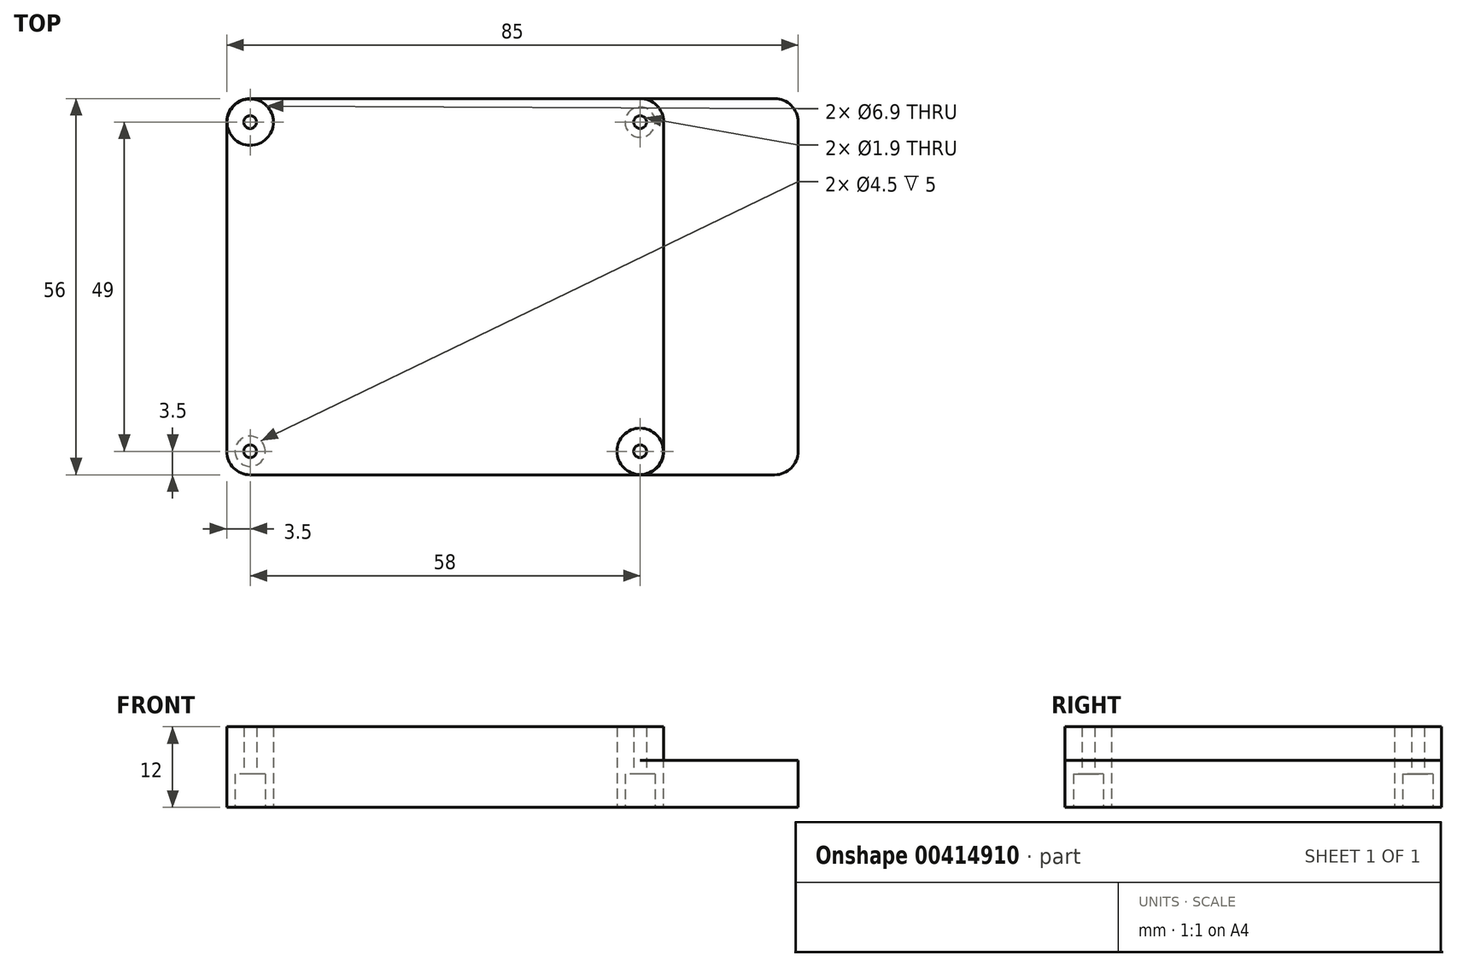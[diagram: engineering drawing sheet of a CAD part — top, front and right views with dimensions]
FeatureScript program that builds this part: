
annotation { "Feature Type Name" : "Feature", "Feature Type Description" : "" }
export const myFeature = defineFeature(function(context is Context, id is Id, definition is map)
    precondition{}
    {
        {
            var Q0;
            Q0=qCreatedBy(makeId("Top.planeOp"),FACE);
            var sketch = newSketch(context, id + "F0", { "sketchPlane" : qUnion([Q0])});
            skLineSegment(sketch, "E0.bottom", {"start": v(3.5, 0) * mm, "end": v(81.5, 0) * mm});
            skLineSegment(sketch, "E0.top", {"start": v(3.5, 56) * mm, "end": v(81.5, 56) * mm});
            skLineSegment(sketch, "E0.left", {"start": v(0, 3.5) * mm, "end": v(0, 52.5) * mm});
            skLineSegment(sketch, "E0.right", {"start": v(85, 3.5) * mm, "end": v(85, 52.5) * mm});
            skPoint(sketch, "E1.visualSharp", {"position": v(0, 56) * mm});
            skArc(sketch, "E1.filletArc", {"start": v(3.5, 56) * mm, "mid": v(1.03, 54.97) * mm, "end": v(0, 52.5) * mm});
            skPoint(sketch, "E2.visualSharp", {"position": v(85, 56) * mm});
            skArc(sketch, "E2.filletArc", {"start": v(85, 52.5) * mm, "mid": v(83.97, 54.97) * mm, "end": v(81.5, 56) * mm});
            skPoint(sketch, "E3.visualSharp", {"position": v(85, 0) * mm});
            skArc(sketch, "E3.filletArc", {"start": v(81.5, 0) * mm, "mid": v(83.97, 1.03) * mm, "end": v(85, 3.5) * mm});
            skPoint(sketch, "E4.visualSharp", {"position": v(0, 0) * mm});
            skArc(sketch, "E4.filletArc", {"start": v(0, 3.5) * mm, "mid": v(1.03, 1.03) * mm, "end": v(3.5, 0) * mm});
            skLineSegment(sketch, "E5", {"start": v(0, 28) * mm, "end": v(85, 28) * mm, "construction": true});
            skLineSegment(sketch, "E6", {"start": v(3.5, 56) * mm, "end": v(3.5, 0) * mm, "construction": true});
            skLineSegment(sketch, "E7", {"start": v(61.5, 56) * mm, "end": v(61.5, 0) * mm, "construction": true});
            skLineSegment(sketch, "E8", {"start": v(-3.04, 52.5) * mm, "end": v(0, 52.5) * mm, "construction": true});
            skLineSegment(sketch, "E9", {"start": v(-4.07, 3.5) * mm, "end": v(0, 3.5) * mm, "construction": true});
            skCircle(sketch, "E10", {"center": v(3.5, 3.5) * mm, "radius": 0.95 * mm});
            skCircle(sketch, "E11", {"center": v(3.5, 3.5) * mm, "radius": 3.45 * mm});
            skCircle(sketch, "E12.MirrorC", {"center": v(3.5, 52.5) * mm, "radius": 3.45 * mm});
            skCircle(sketch, "E13.MirrorC", {"center": v(3.5, 52.5) * mm, "radius": 0.95 * mm});
            skLineSegment(sketch, "E14", {"start": v(32.5, 56) * mm, "end": v(32.5, 0) * mm, "construction": true});
            skCircle(sketch, "E15.MirrorC", {"center": v(61.5, 52.5) * mm, "radius": 3.45 * mm});
            skCircle(sketch, "E16.MirrorC", {"center": v(61.5, 52.5) * mm, "radius": 0.95 * mm});
            skCircle(sketch, "E17.MirrorC", {"center": v(61.5, 3.5) * mm, "radius": 0.95 * mm});
            skCircle(sketch, "E18.MirrorC", {"center": v(61.5, 3.5) * mm, "radius": 3.45 * mm});
            skCircle(sketch, "E19", {"center": v(3.5, 3.5) * mm, "radius": 2.25 * mm});
            skCircle(sketch, "E20.MirrorC", {"center": v(3.5, 52.5) * mm, "radius": 2.25 * mm});
            skCircle(sketch, "E21.MirrorC", {"center": v(61.5, 52.5) * mm, "radius": 2.25 * mm});
            skCircle(sketch, "E22.MirrorC", {"center": v(61.5, 3.5) * mm, "radius": 2.25 * mm});
            skSolve(sketch);
        }
        {
            var Q0;
            Q0=qCreatedBy(makeId("Top.planeOp"),FACE);
            var sketch = newSketch(context, id + "F1", { "sketchPlane" : qUnion([Q0])});
            skLineSegment(sketch, "E23.bottom", {"start": v(3.5, 0) * mm, "end": v(61.5, 0) * mm});
            skLineSegment(sketch, "E23.top", {"start": v(3.5, 56) * mm, "end": v(61.5, 56) * mm});
            skLineSegment(sketch, "E23.left", {"start": v(0, 3.5) * mm, "end": v(0, 52.5) * mm});
            skLineSegment(sketch, "E23.right", {"start": v(65, 3.5) * mm, "end": v(65, 52.5) * mm});
            skPoint(sketch, "E24.visualSharp", {"position": v(0, 56) * mm});
            skArc(sketch, "E24.filletArc", {"start": v(3.5, 56) * mm, "mid": v(1.03, 54.97) * mm, "end": v(0, 52.5) * mm});
            skPoint(sketch, "E25.visualSharp", {"position": v(65, 56) * mm});
            skArc(sketch, "E25.filletArc", {"start": v(65, 52.5) * mm, "mid": v(63.97, 54.97) * mm, "end": v(61.5, 56) * mm});
            skPoint(sketch, "E26.visualSharp", {"position": v(65, 0) * mm});
            skArc(sketch, "E26.filletArc", {"start": v(61.5, 0) * mm, "mid": v(63.97, 1.03) * mm, "end": v(65, 3.5) * mm});
            skPoint(sketch, "E27.visualSharp", {"position": v(0, 0) * mm});
            skArc(sketch, "E27.filletArc", {"start": v(0, 3.5) * mm, "mid": v(1.03, 1.03) * mm, "end": v(3.5, 0) * mm});
            skLineSegment(sketch, "E28", {"start": v(0, 28) * mm, "end": v(65, 28) * mm, "construction": true});
            skLineSegment(sketch, "E29", {"start": v(3.5, 56) * mm, "end": v(3.5, 0) * mm, "construction": true});
            skLineSegment(sketch, "E30", {"start": v(61.5, 56) * mm, "end": v(61.5, 0) * mm, "construction": true});
            skLineSegment(sketch, "E31", {"start": v(-37.6, 52.5) * mm, "end": v(0, 52.5) * mm, "construction": true});
            skLineSegment(sketch, "E32", {"start": v(-38.61, 3.5) * mm, "end": v(0, 3.5) * mm, "construction": true});
            skCircle(sketch, "E33", {"center": v(3.5, 3.5) * mm, "radius": 0.95 * mm});
            skCircle(sketch, "E34", {"center": v(3.5, 3.5) * mm, "radius": 3.45 * mm});
            skCircle(sketch, "E35.MirrorC", {"center": v(3.5, 52.5) * mm, "radius": 3.45 * mm});
            skCircle(sketch, "E36.MirrorC", {"center": v(3.5, 52.5) * mm, "radius": 0.95 * mm});
            skLineSegment(sketch, "E37", {"start": v(32.5, 56) * mm, "end": v(32.5, 0) * mm, "construction": true});
            skCircle(sketch, "E38.MirrorC", {"center": v(61.5, 52.5) * mm, "radius": 3.45 * mm});
            skCircle(sketch, "E39.MirrorC", {"center": v(61.5, 52.5) * mm, "radius": 0.95 * mm});
            skCircle(sketch, "E40.MirrorC", {"center": v(61.5, 3.5) * mm, "radius": 0.95 * mm});
            skCircle(sketch, "E41.MirrorC", {"center": v(61.5, 3.5) * mm, "radius": 3.45 * mm});
            skCircle(sketch, "E42", {"center": v(3.5, 3.5) * mm, "radius": 2.25 * mm});
            skCircle(sketch, "E43.MirrorC", {"center": v(3.5, 52.5) * mm, "radius": 2.25 * mm});
            skCircle(sketch, "E44.MirrorC", {"center": v(61.5, 52.5) * mm, "radius": 2.25 * mm});
            skCircle(sketch, "E45.MirrorC", {"center": v(61.5, 3.5) * mm, "radius": 2.25 * mm});
            skSolve(sketch);
        }
        {
            var Q0;
            Q0=makeQuery(id+"F0.imprint","IMPRINT",FACE,{"disambiguationData":[TD([[makeQuery(id+"F0.imprint","IMPRINT",EDGE,{"derivedFrom":sQuery(id+"F0.wireOp",EDGE,"E0.bottom")}),1.0]])]});
            var Q1;
            Q1=makeQuery(id+"F0.imprint","IMPRINT",FACE,{"disambiguationData":[TD([[makeQuery(id+"F0.imprint","IMPRINT",EDGE,{"derivedFrom":sQuery(id+"F0.wireOp",EDGE,"E12.MirrorC")}),-1.0]])]});
            var Q2;
            Q2 = qSketchRegion(id + "F0", true);
            var Q3;
            Q3=makeQuery(id+"F0.imprint","IMPRINT",FACE,{"disambiguationData":[TD([[makeQuery(id+"F0.imprint","IMPRINT",EDGE,{"derivedFrom":sQuery(id+"F0.wireOp",EDGE,"E15.MirrorC")}),1.0]])]});
            var Q4;
            Q4=makeQuery(id+"F0.imprint","IMPRINT",FACE,{"disambiguationData":[TD([[makeQuery(id+"F0.imprint","IMPRINT",EDGE,{"derivedFrom":sQuery(id+"F0.wireOp",EDGE,"E18.MirrorC")}),-1.0]])]});
            var Q5;
            Q5=makeQuery(id+"F0.imprint","IMPRINT",FACE,{"disambiguationData":[TD([[makeQuery(id+"F0.imprint","IMPRINT",EDGE,{"derivedFrom":sQuery(id+"F0.wireOp",EDGE,"E11")}),1.0]])]});
            extrude(context, id + "F2", {"entities" : qUnion([Q0, Q1, Q2, Q3, Q4, Q5]), "depth" : 2 * mm});
        }
        {
            var Q0;
            Q0=makeQuery(id+"F0.imprint","IMPRINT",FACE,{"disambiguationData":[TD([[makeQuery(id+"F0.imprint","IMPRINT",EDGE,{"derivedFrom":sQuery(id+"F0.wireOp",EDGE,"E11")}),1.0]])]});
            var Q1;
            Q1=makeQuery(id+"F0.imprint","IMPRINT",FACE,{"disambiguationData":[TD([[makeQuery(id+"F0.imprint","IMPRINT",EDGE,{"derivedFrom":sQuery(id+"F0.wireOp",EDGE,"E12.MirrorC")}),-1.0]])]});
            var Q2;
            Q2=makeQuery(id+"F0.imprint","IMPRINT",FACE,{"disambiguationData":[TD([[makeQuery(id+"F0.imprint","IMPRINT",EDGE,{"derivedFrom":sQuery(id+"F0.wireOp",EDGE,"E18.MirrorC")}),-1.0]])]});
            var Q3;
            Q3=makeQuery(id+"F0.imprint","IMPRINT",FACE,{"disambiguationData":[TD([[makeQuery(id+"F0.imprint","IMPRINT",EDGE,{"derivedFrom":sQuery(id+"F0.wireOp",EDGE,"E15.MirrorC")}),1.0]])]});
            var Q4;
            Q4=makeQuery(id+"F0.imprint","IMPRINT",FACE,{"disambiguationData":[TD([[makeQuery(id+"F0.imprint","IMPRINT",EDGE,{"derivedFrom":sQuery(id+"F0.wireOp",EDGE,"E16.MirrorC")}),-1.0]])]});
            var Q5;
            Q5=makeQuery(id+"F0.imprint","IMPRINT",FACE,{"disambiguationData":[TD([[makeQuery(id+"F0.imprint","IMPRINT",EDGE,{"derivedFrom":sQuery(id+"F0.wireOp",EDGE,"E17.MirrorC")}),1.0]])]});
            var Q6;
            Q6=makeQuery(id+"F0.imprint","IMPRINT",FACE,{"disambiguationData":[TD([[makeQuery(id+"F0.imprint","IMPRINT",EDGE,{"derivedFrom":sQuery(id+"F0.wireOp",EDGE,"E10")}),-1.0]])]});
            var Q7;
            Q7=makeQuery(id+"F0.imprint","IMPRINT",FACE,{"disambiguationData":[TD([[makeQuery(id+"F0.imprint","IMPRINT",EDGE,{"derivedFrom":sQuery(id+"F0.wireOp",EDGE,"E13.MirrorC")}),1.0]])]});
            extrude(context, id + "F3", {"entities" : qUnion([Q0, Q1, Q2, Q3, Q4, Q5, Q6, Q7]), "operationType" : NewBodyOperationType.ADD, "depth" : (2 + 5) * mm});
        }
        {
            var Q0;
            Q0=makeQuery(id+"F1.imprint","IMPRINT",FACE,{"disambiguationData":[TD([[makeQuery(id+"F1.imprint","IMPRINT",EDGE,{"derivedFrom":sQuery(id+"F1.wireOp",EDGE,"E34")}),1.0]])]});
            var Q1;
            Q1=makeQuery(id+"F1.imprint","IMPRINT",FACE,{"disambiguationData":[TD([[makeQuery(id+"F1.imprint","IMPRINT",EDGE,{"derivedFrom":sQuery(id+"F1.wireOp",EDGE,"E23.bottom")}),1.0]])]});
            var Q2;
            Q2=makeQuery(id+"F1.imprint","IMPRINT",FACE,{"disambiguationData":[TD([[makeQuery(id+"F1.imprint","IMPRINT",EDGE,{"derivedFrom":sQuery(id+"F1.wireOp",EDGE,"E41.MirrorC")}),-1.0]])]});
            var Q3;
            Q3=makeQuery(id+"F1.imprint","IMPRINT",FACE,{"disambiguationData":[TD([[makeQuery(id+"F1.imprint","IMPRINT",EDGE,{"derivedFrom":sQuery(id+"F1.wireOp",EDGE,"E35.MirrorC")}),-1.0]])]});
            var Q4;
            Q4=makeQuery(id+"F1.imprint","IMPRINT",FACE,{"disambiguationData":[TD([[makeQuery(id+"F1.imprint","IMPRINT",EDGE,{"derivedFrom":sQuery(id+"F1.wireOp",EDGE,"E38.MirrorC")}),1.0]])]});
            extrude(context, id + "F4", {"entities" : qUnion([Q0, Q1, Q2, Q3, Q4]), "depth" : 2 * mm});
        }
        {
            var Q0;
            Q0=makeQuery(id+"F1.imprint","IMPRINT",FACE,{"disambiguationData":[TD([[makeQuery(id+"F1.imprint","IMPRINT",EDGE,{"derivedFrom":sQuery(id+"F1.wireOp",EDGE,"E41.MirrorC")}),-1.0]])]});
            var Q1;
            Q1=makeQuery(id+"F1.imprint","IMPRINT",FACE,{"disambiguationData":[TD([[makeQuery(id+"F1.imprint","IMPRINT",EDGE,{"derivedFrom":sQuery(id+"F1.wireOp",EDGE,"E34")}),1.0]])]});
            var Q2;
            Q2=makeQuery(id+"F1.imprint","IMPRINT",FACE,{"disambiguationData":[TD([[makeQuery(id+"F1.imprint","IMPRINT",EDGE,{"derivedFrom":sQuery(id+"F1.wireOp",EDGE,"E35.MirrorC")}),-1.0]])]});
            var Q3;
            Q3=makeQuery(id+"F1.imprint","IMPRINT",FACE,{"disambiguationData":[TD([[makeQuery(id+"F1.imprint","IMPRINT",EDGE,{"derivedFrom":sQuery(id+"F1.wireOp",EDGE,"E38.MirrorC")}),1.0]])]});
            var Q4;
            Q4=makeQuery(id+"F1.imprint","IMPRINT",FACE,{"disambiguationData":[TD([[makeQuery(id+"F1.imprint","IMPRINT",EDGE,{"derivedFrom":sQuery(id+"F1.wireOp",EDGE,"E40.MirrorC")}),1.0]])]});
            var Q5;
            Q5=makeQuery(id+"F1.imprint","IMPRINT",FACE,{"disambiguationData":[TD([[makeQuery(id+"F1.imprint","IMPRINT",EDGE,{"derivedFrom":sQuery(id+"F1.wireOp",EDGE,"E33")}),-1.0]])]});
            var Q6;
            Q6=makeQuery(id+"F1.imprint","IMPRINT",FACE,{"disambiguationData":[TD([[makeQuery(id+"F1.imprint","IMPRINT",EDGE,{"derivedFrom":sQuery(id+"F1.wireOp",EDGE,"E36.MirrorC")}),1.0]])]});
            var Q7;
            Q7=makeQuery(id+"F1.imprint","IMPRINT",FACE,{"disambiguationData":[TD([[makeQuery(id+"F1.imprint","IMPRINT",EDGE,{"derivedFrom":sQuery(id+"F1.wireOp",EDGE,"E39.MirrorC")}),-1.0]])]});
            extrude(context, id + "F5", {"entities" : qUnion([Q0, Q1, Q2, Q3, Q4, Q5, Q6, Q7]), "operationType" : NewBodyOperationType.ADD, "depth" : (2 + 10) * mm});
        }
        {
            var Q0;
            Q0=makeQuery(id+"F0.imprint","IMPRINT",FACE,{"disambiguationData":[TD([[makeQuery(id+"F0.imprint","IMPRINT",EDGE,{"derivedFrom":sQuery(id+"F0.wireOp",EDGE,"E17.MirrorC")}),-1.0]])]});
            var Q1;
            Q1=makeQuery(id+"F0.imprint","IMPRINT",FACE,{"disambiguationData":[TD([[makeQuery(id+"F0.imprint","IMPRINT",EDGE,{"derivedFrom":sQuery(id+"F0.wireOp",EDGE,"E17.MirrorC")}),1.0]])]});
            var Q2;
            Q2=makeQuery(id+"F0.imprint","IMPRINT",FACE,{"disambiguationData":[TD([[makeQuery(id+"F0.imprint","IMPRINT",EDGE,{"derivedFrom":sQuery(id+"F0.wireOp",EDGE,"E16.MirrorC")}),-1.0]])]});
            var Q3;
            Q3=makeQuery(id+"F0.imprint","IMPRINT",FACE,{"disambiguationData":[TD([[makeQuery(id+"F0.imprint","IMPRINT",EDGE,{"derivedFrom":sQuery(id+"F0.wireOp",EDGE,"E16.MirrorC")}),1.0]])]});
            var Q4;
            Q4=makeQuery(id+"F0.imprint","IMPRINT",FACE,{"disambiguationData":[TD([[makeQuery(id+"F0.imprint","IMPRINT",EDGE,{"derivedFrom":sQuery(id+"F0.wireOp",EDGE,"E13.MirrorC")}),-1.0]])]});
            var Q5;
            Q5=makeQuery(id+"F0.imprint","IMPRINT",FACE,{"disambiguationData":[TD([[makeQuery(id+"F0.imprint","IMPRINT",EDGE,{"derivedFrom":sQuery(id+"F0.wireOp",EDGE,"E13.MirrorC")}),1.0]])]});
            var Q6;
            Q6=makeQuery(id+"F0.imprint","IMPRINT",FACE,{"disambiguationData":[TD([[makeQuery(id+"F0.imprint","IMPRINT",EDGE,{"derivedFrom":sQuery(id+"F0.wireOp",EDGE,"E10")}),1.0]])]});
            var Q7;
            Q7=makeQuery(id+"F0.imprint","IMPRINT",FACE,{"disambiguationData":[TD([[makeQuery(id+"F0.imprint","IMPRINT",EDGE,{"derivedFrom":sQuery(id+"F0.wireOp",EDGE,"E10")}),-1.0]])]});
            extrude(context, id + "F6", {"entities" : qUnion([Q0, Q1, Q2, Q3, Q4, Q5, Q6, Q7]), "operationType" : NewBodyOperationType.REMOVE, "depth" : 4 * mm});
        }
        {
            var Q0;
            Q0=makeQuery(id+"F1.imprint","IMPRINT",FACE,{"disambiguationData":[TD([[makeQuery(id+"F1.imprint","IMPRINT",EDGE,{"derivedFrom":sQuery(id+"F1.wireOp",EDGE,"E40.MirrorC")}),1.0]])]});
            var Q1;
            Q1=makeQuery(id+"F1.imprint","IMPRINT",FACE,{"disambiguationData":[TD([[makeQuery(id+"F1.imprint","IMPRINT",EDGE,{"derivedFrom":sQuery(id+"F1.wireOp",EDGE,"E40.MirrorC")}),-1.0]])]});
            var Q2;
            Q2=makeQuery(id+"F1.imprint","IMPRINT",FACE,{"disambiguationData":[TD([[makeQuery(id+"F1.imprint","IMPRINT",EDGE,{"derivedFrom":sQuery(id+"F1.wireOp",EDGE,"E33")}),-1.0]])]});
            var Q3;
            Q3=makeQuery(id+"F1.imprint","IMPRINT",FACE,{"disambiguationData":[TD([[makeQuery(id+"F1.imprint","IMPRINT",EDGE,{"derivedFrom":sQuery(id+"F1.wireOp",EDGE,"E33")}),1.0]])]});
            var Q4;
            Q4=makeQuery(id+"F1.imprint","IMPRINT",FACE,{"disambiguationData":[TD([[makeQuery(id+"F1.imprint","IMPRINT",EDGE,{"derivedFrom":sQuery(id+"F1.wireOp",EDGE,"E36.MirrorC")}),1.0]])]});
            var Q5;
            Q5=makeQuery(id+"F1.imprint","IMPRINT",FACE,{"disambiguationData":[TD([[makeQuery(id+"F1.imprint","IMPRINT",EDGE,{"derivedFrom":sQuery(id+"F1.wireOp",EDGE,"E36.MirrorC")}),-1.0]])]});
            var Q6;
            Q6=makeQuery(id+"F1.imprint","IMPRINT",FACE,{"disambiguationData":[TD([[makeQuery(id+"F1.imprint","IMPRINT",EDGE,{"derivedFrom":sQuery(id+"F1.wireOp",EDGE,"E39.MirrorC")}),-1.0]])]});
            var Q7;
            Q7=makeQuery(id+"F1.imprint","IMPRINT",FACE,{"disambiguationData":[TD([[makeQuery(id+"F1.imprint","IMPRINT",EDGE,{"derivedFrom":sQuery(id+"F1.wireOp",EDGE,"E39.MirrorC")}),1.0]])]});
            extrude(context, id + "F7", {"entities" : qUnion([Q0, Q1, Q2, Q3, Q4, Q5, Q6, Q7]), "operationType" : NewBodyOperationType.REMOVE, "depth" : 5 * mm});
        }
    });
